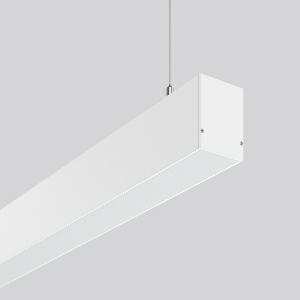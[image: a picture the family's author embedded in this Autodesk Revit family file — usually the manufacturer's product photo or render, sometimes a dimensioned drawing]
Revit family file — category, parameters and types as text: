
# Revit family: less_is_more_50_312321_002_1_76_139a
name_source: partatom
category: Lighting Fixtures
units: mm (PartAtom-declared; Revit-internal decimal feet)

## family parameters
Cut with Voids When Loaded = No
Host = Face
Light Source = No
Part Type = Normal
Room Calculation Point = No
Round Connector Dimension = Use Diameter
Shared = No

## types (1)
- LESS IS MORE 50 (1 x LED Modul 840, 8850 lm, 4000)
    Apparent Load = 74 VA
    CIE Flux Codes = 49 80 96 63 100
    Color Rendering = 80
    Color Temperature = 4000
    Default Elevation = 1800 mm
    Description = Series: LESS IS MORE 50
Linear pendant luminaire for aesthetically sophisticated lighting. Housing: extruded aluminium profile, powder-coated. End cap aluminium powder-coated. Canopy made of aluminium, powder-coated. Diffuser made of non-yellowing plastic (PMMA), opal. Direct 65%, indirect 35% light emission. Controlled separately. Suitable for pendant. 2-point steel cable suspension freely positionable and infinitely height-adjustable. Special lengths available on request. LED unit with integrated converter interchangeable and removable. Suitable for through-wiring. With sensors or as a safety luminaire on request. 
Colour: traffic white, matt (RAL 9016)
Length: 1967 mm
Width: 57 mm
Height: 75 mm
Suspension length: 2000 mm
Lamp: LED
Socket: without socket
Colour temperature: 4000K
Colour rendering index (CRI): 80
Light source: LED
Socket lamp2: Without base
Colour temperature: 4000K
System power: 74 W
Rated luminous flux: 8850 lm
Luminous efficiency: 120 lm/W
Control gear: Converter, dimmable, DALI
Control gear: Converter, dimmable, DALI
Protection class: I
Type of protection: IP 20
    Height = 75 mm
    Lamp = 1 x LED Modul 840
    Lamp Light Flux = 8850 lm
    Lamp count = 1
    Length = 1967 mm
    Lifetime = 50000 h
    Luminous efficacy = 120 lm/W
    Manufacturer = RZB
    ModVariant = No
    Model = 312321.002.1.76
    Mounting Place = Ceiling
    Mounting Type = Pendant
    Number of Poles = 1
    OnlyDefault = Yes
    Power Factor = 1
    Product Name = LESS IS MORE 50
    Product group = Pendant LED linear luminaires
    ProductGroupID = 907
    Protection Class = Protection class I
    Protection Degree = IP 20
    RLX_Detail_Level = 1
    RLX_Emergency_Light_Flux = 0 lm
    RLX_Emergency_Type = 0
    RLX_Emergency_Type_DB = No
    RlxData = <blob elided: 31677 chars, md5=bf278cd4>
    Socket = socket
    Standby Power = 0 W
    System Light Flux = 8850 lm
    System Power = 74 W
    Type Comments = Product without accessories
    Type Image = 312318.002.jpg
    URL = http://relux.com
    VarID = ---
    Voltage = 230 V
    Voltage Range = 220-240 V
    Weight = 0.00 kg
    Width = 57 mm

## geometry (parser evidence)
native form markers: Blend x4, Sweep x13
no freeform markers — native parametric forms only
